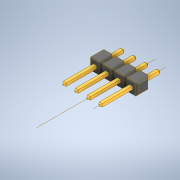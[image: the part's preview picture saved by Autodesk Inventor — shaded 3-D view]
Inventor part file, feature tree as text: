
AUTODESK INVENTOR PART (.ipt)
format: ipt  version: 2020 (Build 240168000, 168)  size: 278,528 bytes
history: native  units: in
note: dims shown in document units (in); Inventor stores cm internally (conversion verified against a paired STEP export)
features: other x9, plane x3
ambient origin geometry x8: Origin, YZ Plane, XZ Plane, XY Plane, X Axis, Y Axis, Z Axis, Center Point
bodies: Solid1 (feature_tree), Solid2 (feature_tree), Solid3 (feature_tree), Solid4 (feature_tree)
feature tree (12):
  other  "Repaired Geometry1"
  plane  "Work Plane1"
  plane  "Work Plane2"
  other  "Work Axis1"
  other  "Work Axis2"
  plane  "Work Plane3"
  other  "brep_1"
  other  "brep_2"
  other  "brep_3"
  other  "brep_4"
  other  "Composite1"
  other  "Srf1"
